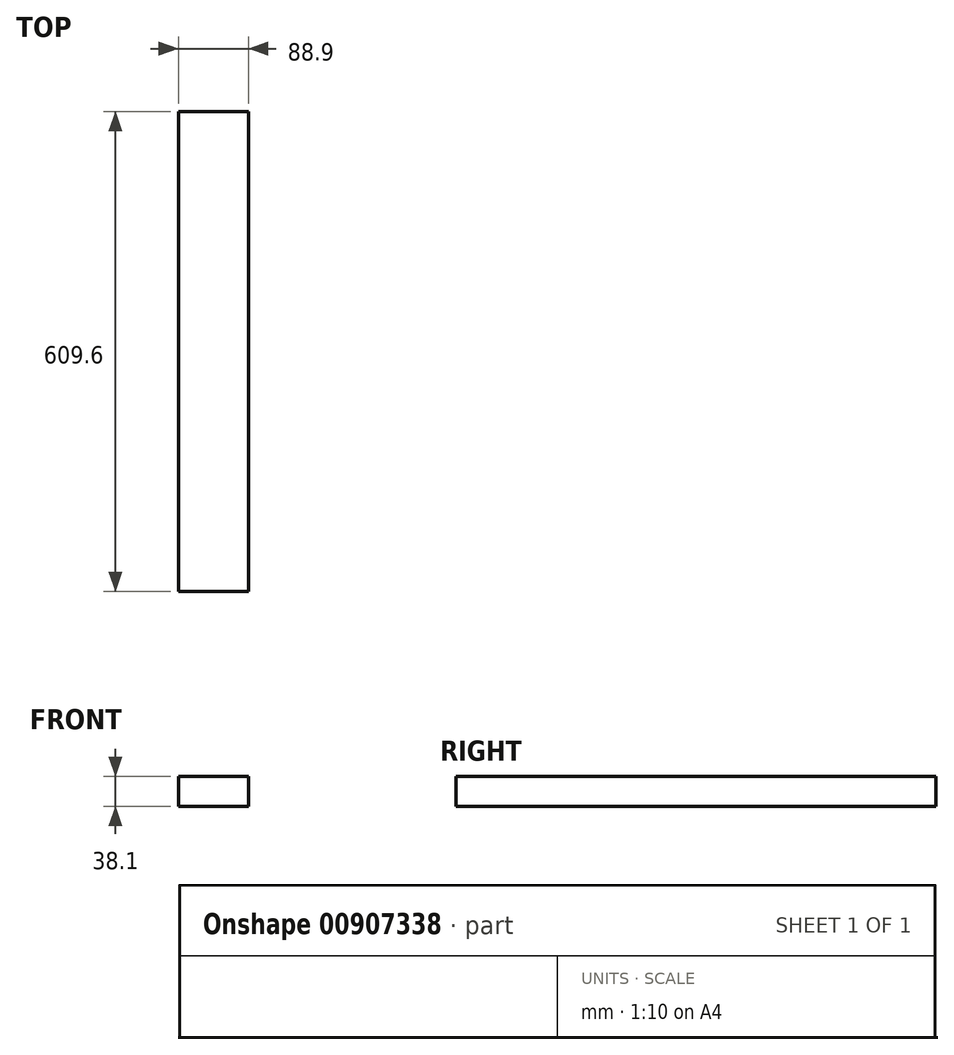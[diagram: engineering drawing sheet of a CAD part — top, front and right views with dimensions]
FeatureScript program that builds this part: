
annotation { "Feature Type Name" : "Feature", "Feature Type Description" : "" }
export const myFeature = defineFeature(function(context is Context, id is Id, definition is map)
    precondition{}
    {
        {
            var Q0;
            Q0=qCreatedBy(makeId("Front.planeOp"),FACE);
            var sketch = newSketch(context, id + "F0", { "sketchPlane" : qUnion([Q0])});
            skLineSegment(sketch, "E0.bottom", {"start": v(-44.45, 19.05) * mm, "end": v(44.45, 19.05) * mm});
            skLineSegment(sketch, "E0.top", {"start": v(-44.45, -19.05) * mm, "end": v(44.45, -19.05) * mm});
            skLineSegment(sketch, "E0.left", {"start": v(-44.45, 19.05) * mm, "end": v(-44.45, -19.05) * mm});
            skLineSegment(sketch, "E0.right", {"start": v(44.45, 19.05) * mm, "end": v(44.45, -19.05) * mm});
            skPoint(sketch, "E0.middle", {"position": v(0, 0) * mm});
            skSolve(sketch);
        }
        {
            var Q0;
            Q0=makeQuery(id+"F0.imprint","IMPRINT",FACE,{"disambiguationData":[TD([[makeQuery(id+"F0.imprint","IMPRINT",EDGE,{"derivedFrom":sQuery(id+"F0.wireOp",EDGE,"E0.bottom")}),-1.0]])]});
            extrude(context, id + "F1", {"entities" : qUnion([Q0]), "endBound" : BoundingType.SYMMETRIC, "depth" : 609.6 * mm, "offsetDistance" : 25.4 * mm});
        }
    });
